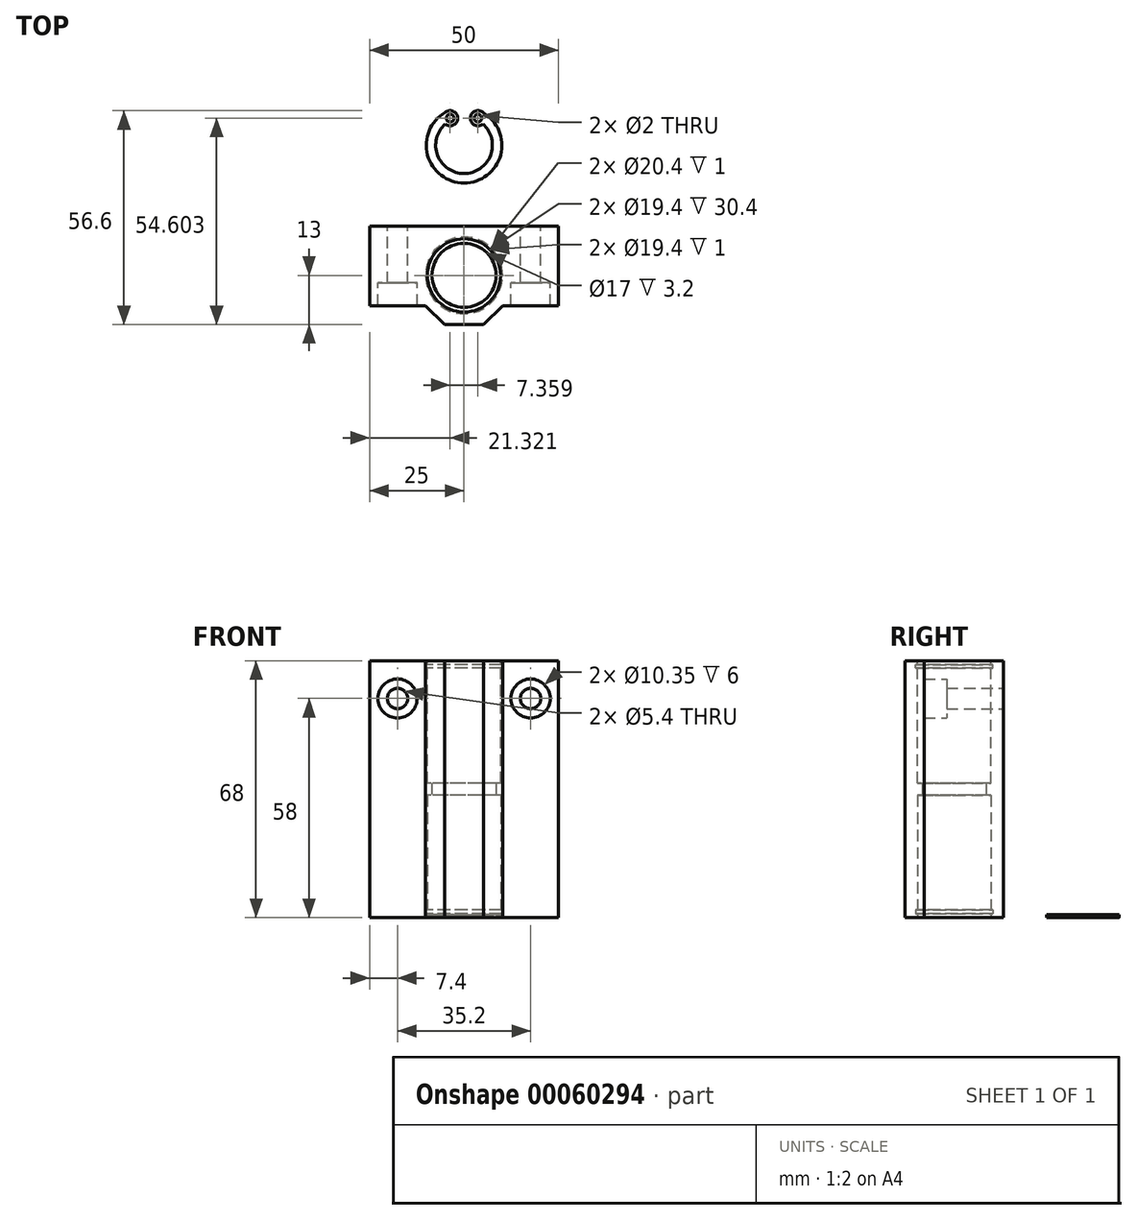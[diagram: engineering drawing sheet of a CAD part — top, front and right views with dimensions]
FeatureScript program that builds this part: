
annotation { "Feature Type Name" : "Feature", "Feature Type Description" : "" }
export const myFeature = defineFeature(function(context is Context, id is Id, definition is map)
    precondition{}
    {
        {
            var Q0;
            Q0=qCreatedBy(makeId("Top.planeOp"),FACE);
            var sketch = newSketch(context, id + "F0", { "sketchPlane" : qUnion([Q0])});
            skLineSegment(sketch, "E0.bottom", {"start": v(-25, 13) * mm, "end": v(25, 13) * mm});
            skLineSegment(sketch, "E0.top", {"start": v(-25, -13) * mm, "end": v(25, -13) * mm});
            skLineSegment(sketch, "E0.left", {"start": v(-25, 13) * mm, "end": v(-25, -13) * mm});
            skLineSegment(sketch, "E0.right", {"start": v(25, 13) * mm, "end": v(25, -13) * mm});
            skLineSegment(sketch, "E1", {"start": v(-25, 0) * mm, "end": v(25, 0) * mm});
            skLineSegment(sketch, "E2", {"start": v(-25, -8) * mm, "end": v(25, -8) * mm});
            skLineSegment(sketch, "E3", {"start": v(-25, 5) * mm, "end": v(-23, 3) * mm});
            skLineSegment(sketch, "E4", {"start": v(-23, 3) * mm, "end": v(-23, -13) * mm});
            skCircle(sketch, "E5", {"center": v(0, 0) * mm, "radius": 10.2 * mm});
            skLineSegment(sketch, "E6", {"start": v(0, 13) * mm, "end": v(0, -13) * mm});
            skLineSegment(sketch, "E7.MirrorCS", {"start": v(25, 5) * mm, "end": v(23, 3) * mm});
            skLineSegment(sketch, "E8.MirrorCS", {"start": v(23, 3) * mm, "end": v(23, -13) * mm});
            skLineSegment(sketch, "E9", {"start": v(-25, 5) * mm, "end": v(-25, 3) * mm});
            skLineSegment(sketch, "E10", {"start": v(25, 5) * mm, "end": v(25, 3) * mm});
            skLineSegment(sketch, "E11", {"start": v(-10.2, 13) * mm, "end": v(-10.2, -13) * mm});
            skLineSegment(sketch, "E12.MirrorCS", {"start": v(10.2, 13) * mm, "end": v(10.2, -13) * mm});
            skLineSegment(sketch, "E13", {"start": v(-10.2, -8) * mm, "end": v(-5.2, -13) * mm});
            skLineSegment(sketch, "E14.MirrorCS", {"start": v(10.2, -8) * mm, "end": v(5.2, -13) * mm});
            skCircle(sketch, "E15", {"center": v(0, 0) * mm, "radius": 9.7 * mm});
            skCircle(sketch, "E16", {"center": v(0, 0) * mm, "radius": 8.5 * mm});
            skSolve(sketch);
        }
        {
            var Q0;
            {var subQ0=sQuery(id+"F0.wireOp",EDGE,"E3");Q0=makeQuery(id+"F0.imprint","IMPRINT",FACE,{"disambiguationData":[TD([[makeQuery(id+"F0.imprint","IMPRINT",EDGE,{"derivedFrom":subQ0}),1.0]])]});}
            var Q1;
            {var subQ0=sQuery(id+"F0.wireOp",EDGE,"E6");var subQ1=sQuery(id+"F0.wireOp",EDGE,"E0.bottom");var subQ2=makeQuery(id+"F0.imprint","INTERSECT",VERTEX,{"derivedFrom":[subQ1,subQ0]});Q1=makeQuery(id+"F0.imprint","IMPRINT",FACE,{"disambiguationData":[TD([[makeQuery(id+"F0.imprint","IMPRINT",EDGE,{"disambiguationData":[TD([[subQ2,1.0]])],"derivedFrom":subQ1}),-1.0]])]});}
            var Q2;
            {var subQ0=sQuery(id+"F0.wireOp",EDGE,"E6");var subQ1=sQuery(id+"F0.wireOp",EDGE,"E0.bottom");var subQ2=makeQuery(id+"F0.imprint","INTERSECT",VERTEX,{"derivedFrom":[subQ1,subQ0]});Q2=makeQuery(id+"F0.imprint","IMPRINT",FACE,{"disambiguationData":[TD([[makeQuery(id+"F0.imprint","IMPRINT",EDGE,{"disambiguationData":[TD([[subQ2,-1.0]])],"derivedFrom":subQ1}),-1.0]])]});}
            var Q3;
            {var subQ0=sQuery(id+"F0.wireOp",EDGE,"E7.MirrorCS");Q3=makeQuery(id+"F0.imprint","IMPRINT",FACE,{"disambiguationData":[TD([[makeQuery(id+"F0.imprint","IMPRINT",EDGE,{"derivedFrom":subQ0}),-1.0]])]});}
            var Q4;
            {var subQ7=sQuery(id+"F0.wireOp",EDGE,"E13");Q4=makeQuery(id+"F0.imprint","IMPRINT",FACE,{"disambiguationData":[TD([[makeQuery(id+"F0.imprint","IMPRINT",EDGE,{"derivedFrom":subQ7}),1.0]])]});}
            var Q5;
            {var subQ0=sQuery(id+"F0.wireOp",EDGE,"E4");var subQ1=sQuery(id+"F0.wireOp",EDGE,"E1");var subQ2=makeQuery(id+"F0.imprint","INTERSECT",VERTEX,{"derivedFrom":[subQ1,subQ0]});Q5=makeQuery(id+"F0.imprint","IMPRINT",FACE,{"disambiguationData":[TD([[makeQuery(id+"F0.imprint","IMPRINT",EDGE,{"disambiguationData":[TD([[subQ2,-1.0]])],"derivedFrom":subQ0}),1.0]])]});}
            var Q6;
            {var subQ1=sQuery(id+"F0.wireOp",EDGE,"E2");var subQ3=sQuery(id+"F0.wireOp",EDGE,"E5");var subQ4=makeQuery(id+"F0.imprint","INTERSECT",VERTEX,{"disambiguationData":[OD(0.0)],"derivedFrom":[subQ1,subQ3]});Q6=makeQuery(id+"F0.imprint","IMPRINT",FACE,{"disambiguationData":[TD([[makeQuery(id+"F0.imprint","IMPRINT",EDGE,{"disambiguationData":[TD([[subQ4,1.0]])],"derivedFrom":subQ1}),1.0]])]});}
            var Q7;
            {var subQ0=sQuery(id+"F0.wireOp",EDGE,"E8.MirrorCS");var subQ1=sQuery(id+"F0.wireOp",EDGE,"E1");var subQ2=makeQuery(id+"F0.imprint","INTERSECT",VERTEX,{"derivedFrom":[subQ1,subQ0]});Q7=makeQuery(id+"F0.imprint","IMPRINT",FACE,{"disambiguationData":[TD([[makeQuery(id+"F0.imprint","IMPRINT",EDGE,{"disambiguationData":[TD([[subQ2,-1.0]])],"derivedFrom":subQ0}),-1.0]])]});}
            var Q8;
            {var subQ1=sQuery(id+"F0.wireOp",EDGE,"E2");var subQ3=sQuery(id+"F0.wireOp",EDGE,"E5");var subQ4=makeQuery(id+"F0.imprint","INTERSECT",VERTEX,{"disambiguationData":[OD(1.0)],"derivedFrom":[subQ1,subQ3]});Q8=makeQuery(id+"F0.imprint","IMPRINT",FACE,{"disambiguationData":[TD([[makeQuery(id+"F0.imprint","IMPRINT",EDGE,{"disambiguationData":[TD([[subQ4,-1.0]])],"derivedFrom":subQ1}),1.0]])]});}
            var Q9;
            {var subQ5=sQuery(id+"F0.wireOp",EDGE,"E14.MirrorCS");Q9=makeQuery(id+"F0.imprint","IMPRINT",FACE,{"disambiguationData":[TD([[makeQuery(id+"F0.imprint","IMPRINT",EDGE,{"derivedFrom":subQ5}),-1.0]])]});}
            var Q10;
            {var subQ3=sQuery(id+"F0.wireOp",EDGE,"E5");var subQ5=sQuery(id+"F0.wireOp",EDGE,"E2");var subQ6=makeQuery(id+"F0.imprint","INTERSECT",VERTEX,{"disambiguationData":[OD(0.0)],"derivedFrom":[subQ5,subQ3]});Q10=makeQuery(id+"F0.imprint","IMPRINT",FACE,{"disambiguationData":[TD([[makeQuery(id+"F0.imprint","IMPRINT",EDGE,{"disambiguationData":[TD([[subQ6,-1.0]])],"derivedFrom":subQ5}),1.0]])]});}
            var Q11;
            {var subQ0=sQuery(id+"F0.wireOp",EDGE,"E5");var subQ1=sQuery(id+"F0.wireOp",EDGE,"E2");var subQ2=makeQuery(id+"F0.imprint","INTERSECT",VERTEX,{"disambiguationData":[OD(0.0)],"derivedFrom":[subQ1,subQ0]});Q11=makeQuery(id+"F0.imprint","IMPRINT",FACE,{"disambiguationData":[TD([[makeQuery(id+"F0.imprint","IMPRINT",EDGE,{"disambiguationData":[TD([[subQ2,-1.0]])],"derivedFrom":subQ1}),-1.0]])]});}
            var Q12;
            {var subQ0=sQuery(id+"F0.wireOp",EDGE,"E15");var subQ1=sQuery(id+"F0.wireOp",EDGE,"E2");var subQ2=makeQuery(id+"F0.imprint","INTERSECT",VERTEX,{"disambiguationData":[OD(1.0)],"derivedFrom":[subQ1,subQ0]});Q12=makeQuery(id+"F0.imprint","IMPRINT",FACE,{"disambiguationData":[TD([[makeQuery(id+"F0.imprint","IMPRINT",EDGE,{"disambiguationData":[TD([[subQ2,-1.0]])],"derivedFrom":subQ1}),-1.0]])]});}
            var Q13;
            {var subQ0=sQuery(id+"F0.wireOp",EDGE,"E15");var subQ5=sQuery(id+"F0.wireOp",EDGE,"E2");var subQ6=makeQuery(id+"F0.imprint","INTERSECT",VERTEX,{"disambiguationData":[OD(1.0)],"derivedFrom":[subQ5,subQ0]});Q13=makeQuery(id+"F0.imprint","IMPRINT",FACE,{"disambiguationData":[TD([[makeQuery(id+"F0.imprint","IMPRINT",EDGE,{"disambiguationData":[TD([[subQ6,-1.0]])],"derivedFrom":subQ5}),1.0]])]});}
            var Q14;
            {var subQ3=sQuery(id+"F0.wireOp",EDGE,"E5");var subQ5=sQuery(id+"F0.wireOp",EDGE,"E6");var subQ6=makeQuery(id+"F0.imprint","INTERSECT",VERTEX,{"disambiguationData":[OD(0.0)],"derivedFrom":[subQ3,subQ5]});Q14=makeQuery(id+"F0.imprint","IMPRINT",FACE,{"disambiguationData":[TD([[makeQuery(id+"F0.imprint","IMPRINT",EDGE,{"disambiguationData":[TD([[subQ6,-1.0]])],"derivedFrom":subQ5}),1.0]])]});}
            var Q15;
            {var subQ3=sQuery(id+"F0.wireOp",EDGE,"E5");var subQ5=sQuery(id+"F0.wireOp",EDGE,"E6");var subQ6=makeQuery(id+"F0.imprint","INTERSECT",VERTEX,{"disambiguationData":[OD(0.0)],"derivedFrom":[subQ3,subQ5]});Q15=makeQuery(id+"F0.imprint","IMPRINT",FACE,{"disambiguationData":[TD([[makeQuery(id+"F0.imprint","IMPRINT",EDGE,{"disambiguationData":[TD([[subQ6,-1.0]])],"derivedFrom":subQ5}),-1.0]])]});}
            var Q16;
            {var subQ0=sQuery(id+"F0.wireOp",EDGE,"E15");var subQ1=sQuery(id+"F0.wireOp",EDGE,"E1");var subQ2=makeQuery(id+"F0.imprint","INTERSECT",VERTEX,{"disambiguationData":[OD(0.0)],"derivedFrom":[subQ1,subQ0]});Q16=makeQuery(id+"F0.imprint","IMPRINT",FACE,{"disambiguationData":[TD([[makeQuery(id+"F0.imprint","IMPRINT",EDGE,{"disambiguationData":[TD([[subQ2,-1.0]])],"derivedFrom":subQ1}),1.0]])]});}
            var Q17;
            {var subQ0=sQuery(id+"F0.wireOp",EDGE,"E15");var subQ1=sQuery(id+"F0.wireOp",EDGE,"E1");var subQ2=makeQuery(id+"F0.imprint","INTERSECT",VERTEX,{"disambiguationData":[OD(0.0)],"derivedFrom":[subQ1,subQ0]});Q17=makeQuery(id+"F0.imprint","IMPRINT",FACE,{"disambiguationData":[TD([[makeQuery(id+"F0.imprint","IMPRINT",EDGE,{"disambiguationData":[TD([[subQ2,-1.0]])],"derivedFrom":subQ1}),-1.0]])]});}
            var Q18;
            {var subQ0=sQuery(id+"F0.wireOp",EDGE,"E15");var subQ1=sQuery(id+"F0.wireOp",EDGE,"E2");var subQ2=makeQuery(id+"F0.imprint","INTERSECT",VERTEX,{"disambiguationData":[OD(0.0)],"derivedFrom":[subQ1,subQ0]});Q18=makeQuery(id+"F0.imprint","IMPRINT",FACE,{"disambiguationData":[TD([[makeQuery(id+"F0.imprint","IMPRINT",EDGE,{"disambiguationData":[TD([[subQ2,-1.0]])],"derivedFrom":subQ1}),-1.0]])]});}
            var Q19;
            {var subQ0=sQuery(id+"F0.wireOp",EDGE,"E16");var subQ1=sQuery(id+"F0.wireOp",EDGE,"E2");var subQ2=makeQuery(id+"F0.imprint","INTERSECT",VERTEX,{"disambiguationData":[OD(1.0)],"derivedFrom":[subQ1,subQ0]});Q19=makeQuery(id+"F0.imprint","IMPRINT",FACE,{"disambiguationData":[TD([[makeQuery(id+"F0.imprint","IMPRINT",EDGE,{"disambiguationData":[TD([[subQ2,-1.0]])],"derivedFrom":subQ1}),-1.0]])]});}
            var Q20;
            {var subQ0=sQuery(id+"F0.wireOp",EDGE,"E16");var subQ1=sQuery(id+"F0.wireOp",EDGE,"E1");var subQ2=makeQuery(id+"F0.imprint","INTERSECT",VERTEX,{"disambiguationData":[OD(1.0)],"derivedFrom":[subQ1,subQ0]});Q20=makeQuery(id+"F0.imprint","IMPRINT",FACE,{"disambiguationData":[TD([[makeQuery(id+"F0.imprint","IMPRINT",EDGE,{"disambiguationData":[TD([[subQ2,-1.0]])],"derivedFrom":subQ1}),-1.0]])]});}
            var Q21;
            {var subQ0=sQuery(id+"F0.wireOp",EDGE,"E16");var subQ1=sQuery(id+"F0.wireOp",EDGE,"E1");var subQ2=makeQuery(id+"F0.imprint","INTERSECT",VERTEX,{"disambiguationData":[OD(1.0)],"derivedFrom":[subQ1,subQ0]});Q21=makeQuery(id+"F0.imprint","IMPRINT",FACE,{"disambiguationData":[TD([[makeQuery(id+"F0.imprint","IMPRINT",EDGE,{"disambiguationData":[TD([[subQ2,-1.0]])],"derivedFrom":subQ1}),1.0]])]});}
            var Q22;
            {var subQ0=sQuery(id+"F0.wireOp",EDGE,"E1");var subQ1=sQuery(id+"F0.wireOp",EDGE,"E0.right");var subQ2=makeQuery(id+"F0.imprint","INTERSECT",VERTEX,{"derivedFrom":[subQ1,subQ0]});Q22=makeQuery(id+"F0.imprint","IMPRINT",FACE,{"disambiguationData":[TD([[makeQuery(id+"F0.imprint","IMPRINT",EDGE,{"disambiguationData":[TD([[subQ2,-1.0]])],"derivedFrom":subQ1}),-1.0]])]});}
            var Q23;
            {var subQ1=sQuery(id+"F0.wireOp",EDGE,"E7.MirrorCS");Q23=makeQuery(id+"F0.imprint","IMPRINT",FACE,{"disambiguationData":[TD([[makeQuery(id+"F0.imprint","IMPRINT",EDGE,{"derivedFrom":subQ1}),1.0]])]});}
            var Q24;
            {var subQ0=sQuery(id+"F0.wireOp",EDGE,"E1");var subQ1=sQuery(id+"F0.wireOp",EDGE,"E0.left");var subQ2=makeQuery(id+"F0.imprint","INTERSECT",VERTEX,{"derivedFrom":[subQ1,subQ0]});Q24=makeQuery(id+"F0.imprint","IMPRINT",FACE,{"disambiguationData":[TD([[makeQuery(id+"F0.imprint","IMPRINT",EDGE,{"disambiguationData":[TD([[subQ2,-1.0]])],"derivedFrom":subQ1}),1.0]])]});}
            var Q25;
            {var subQ5=sQuery(id+"F0.wireOp",EDGE,"E3");Q25=makeQuery(id+"F0.imprint","IMPRINT",FACE,{"disambiguationData":[TD([[makeQuery(id+"F0.imprint","IMPRINT",EDGE,{"derivedFrom":subQ5}),-1.0]])]});}
            extrude(context, id + "F1", {"entities" : qUnion([Q0, Q1, Q2, Q3, Q4, Q5, Q6, Q7, Q8, Q9, Q10, Q11, Q12, Q13, Q14, Q15, Q16, Q17, Q18, Q19, Q20, Q21, Q22, Q23, Q24, Q25]), "depth" : 68 * mm});
        }
        {
            var Q0;
            {var subQ0=sQuery(id+"F0.wireOp",EDGE,"E15");var subQ1=sQuery(id+"F0.wireOp",EDGE,"E1");var subQ2=makeQuery(id+"F0.imprint","INTERSECT",VERTEX,{"disambiguationData":[OD(0.0)],"derivedFrom":[subQ1,subQ0]});Q0=makeQuery(id+"F0.imprint","IMPRINT",FACE,{"disambiguationData":[TD([[makeQuery(id+"F0.imprint","IMPRINT",EDGE,{"disambiguationData":[TD([[subQ2,-1.0]])],"derivedFrom":subQ1}),-1.0]])]});}
            var Q1;
            {var subQ0=sQuery(id+"F0.wireOp",EDGE,"E15");var subQ1=sQuery(id+"F0.wireOp",EDGE,"E2");var subQ2=makeQuery(id+"F0.imprint","INTERSECT",VERTEX,{"disambiguationData":[OD(0.0)],"derivedFrom":[subQ1,subQ0]});Q1=makeQuery(id+"F0.imprint","IMPRINT",FACE,{"disambiguationData":[TD([[makeQuery(id+"F0.imprint","IMPRINT",EDGE,{"disambiguationData":[TD([[subQ2,-1.0]])],"derivedFrom":subQ1}),-1.0]])]});}
            var Q2;
            {var subQ0=sQuery(id+"F0.wireOp",EDGE,"E16");var subQ1=sQuery(id+"F0.wireOp",EDGE,"E2");var subQ2=makeQuery(id+"F0.imprint","INTERSECT",VERTEX,{"disambiguationData":[OD(1.0)],"derivedFrom":[subQ1,subQ0]});Q2=makeQuery(id+"F0.imprint","IMPRINT",FACE,{"disambiguationData":[TD([[makeQuery(id+"F0.imprint","IMPRINT",EDGE,{"disambiguationData":[TD([[subQ2,-1.0]])],"derivedFrom":subQ1}),-1.0]])]});}
            var Q3;
            {var subQ0=sQuery(id+"F0.wireOp",EDGE,"E16");var subQ1=sQuery(id+"F0.wireOp",EDGE,"E1");var subQ2=makeQuery(id+"F0.imprint","INTERSECT",VERTEX,{"disambiguationData":[OD(1.0)],"derivedFrom":[subQ1,subQ0]});Q3=makeQuery(id+"F0.imprint","IMPRINT",FACE,{"disambiguationData":[TD([[makeQuery(id+"F0.imprint","IMPRINT",EDGE,{"disambiguationData":[TD([[subQ2,-1.0]])],"derivedFrom":subQ1}),-1.0]])]});}
            var Q4;
            {var subQ0=sQuery(id+"F0.wireOp",EDGE,"E16");var subQ1=sQuery(id+"F0.wireOp",EDGE,"E1");var subQ2=makeQuery(id+"F0.imprint","INTERSECT",VERTEX,{"disambiguationData":[OD(1.0)],"derivedFrom":[subQ1,subQ0]});Q4=makeQuery(id+"F0.imprint","IMPRINT",FACE,{"disambiguationData":[TD([[makeQuery(id+"F0.imprint","IMPRINT",EDGE,{"disambiguationData":[TD([[subQ2,-1.0]])],"derivedFrom":subQ1}),1.0]])]});}
            var Q5;
            {var subQ0=sQuery(id+"F0.wireOp",EDGE,"E15");var subQ1=sQuery(id+"F0.wireOp",EDGE,"E1");var subQ2=makeQuery(id+"F0.imprint","INTERSECT",VERTEX,{"disambiguationData":[OD(0.0)],"derivedFrom":[subQ1,subQ0]});Q5=makeQuery(id+"F0.imprint","IMPRINT",FACE,{"disambiguationData":[TD([[makeQuery(id+"F0.imprint","IMPRINT",EDGE,{"disambiguationData":[TD([[subQ2,-1.0]])],"derivedFrom":subQ1}),1.0]])]});}
            extrude(context, id + "F2", {"entities" : qUnion([Q0, Q1, Q2, Q3, Q4, Q5]), "operationType" : NewBodyOperationType.REMOVE, "depth" : 32.4 * mm});
        }
        {
            var Q0;
            {var subQ0=sQuery(id+"F0.wireOp",EDGE,"E15");var subQ1=sQuery(id+"F0.wireOp",EDGE,"E2");var subQ2=makeQuery(id+"F0.imprint","INTERSECT",VERTEX,{"disambiguationData":[OD(1.0)],"derivedFrom":[subQ1,subQ0]});Q0=makeQuery(id+"F0.imprint","IMPRINT",FACE,{"disambiguationData":[TD([[makeQuery(id+"F0.imprint","IMPRINT",EDGE,{"disambiguationData":[TD([[subQ2,-1.0]])],"derivedFrom":subQ1}),-1.0]])]});}
            var Q1;
            {var subQ0=sQuery(id+"F0.wireOp",EDGE,"E15");var subQ5=sQuery(id+"F0.wireOp",EDGE,"E2");var subQ6=makeQuery(id+"F0.imprint","INTERSECT",VERTEX,{"disambiguationData":[OD(1.0)],"derivedFrom":[subQ5,subQ0]});Q1=makeQuery(id+"F0.imprint","IMPRINT",FACE,{"disambiguationData":[TD([[makeQuery(id+"F0.imprint","IMPRINT",EDGE,{"disambiguationData":[TD([[subQ6,-1.0]])],"derivedFrom":subQ5}),1.0]])]});}
            var Q2;
            {var subQ3=sQuery(id+"F0.wireOp",EDGE,"E5");var subQ5=sQuery(id+"F0.wireOp",EDGE,"E6");var subQ7=makeQuery(id+"F0.imprint","INTERSECT",VERTEX,{"disambiguationData":[OD(0.0)],"derivedFrom":[subQ3,subQ5]});Q2=makeQuery(id+"F0.imprint","IMPRINT",FACE,{"disambiguationData":[TD([[makeQuery(id+"F0.imprint","IMPRINT",EDGE,{"disambiguationData":[TD([[subQ7,-1.0]])],"derivedFrom":subQ5}),1.0]])]});}
            var Q3;
            {var subQ3=sQuery(id+"F0.wireOp",EDGE,"E5");var subQ5=sQuery(id+"F0.wireOp",EDGE,"E6");var subQ6=makeQuery(id+"F0.imprint","INTERSECT",VERTEX,{"disambiguationData":[OD(0.0)],"derivedFrom":[subQ3,subQ5]});Q3=makeQuery(id+"F0.imprint","IMPRINT",FACE,{"disambiguationData":[TD([[makeQuery(id+"F0.imprint","IMPRINT",EDGE,{"disambiguationData":[TD([[subQ6,-1.0]])],"derivedFrom":subQ5}),-1.0]])]});}
            var Q4;
            {var subQ3=sQuery(id+"F0.wireOp",EDGE,"E5");var subQ5=sQuery(id+"F0.wireOp",EDGE,"E2");var subQ6=makeQuery(id+"F0.imprint","INTERSECT",VERTEX,{"disambiguationData":[OD(0.0)],"derivedFrom":[subQ5,subQ3]});Q4=makeQuery(id+"F0.imprint","IMPRINT",FACE,{"disambiguationData":[TD([[makeQuery(id+"F0.imprint","IMPRINT",EDGE,{"disambiguationData":[TD([[subQ6,-1.0]])],"derivedFrom":subQ5}),1.0]])]});}
            var Q5;
            {var subQ0=sQuery(id+"F0.wireOp",EDGE,"E5");var subQ1=sQuery(id+"F0.wireOp",EDGE,"E2");var subQ2=makeQuery(id+"F0.imprint","INTERSECT",VERTEX,{"disambiguationData":[OD(0.0)],"derivedFrom":[subQ1,subQ0]});Q5=makeQuery(id+"F0.imprint","IMPRINT",FACE,{"disambiguationData":[TD([[makeQuery(id+"F0.imprint","IMPRINT",EDGE,{"disambiguationData":[TD([[subQ2,-1.0]])],"derivedFrom":subQ1}),-1.0]])]});}
            extrude(context, id + "F3", {"entities" : qUnion([Q0, Q1, Q2, Q3, Q4, Q5]), "operationType" : NewBodyOperationType.REMOVE, "depth" : 2 * mm});
        }
        {
            var Q0;
            {var subQ3=sQuery(id+"F0.wireOp",EDGE,"E5");var subQ5=sQuery(id+"F0.wireOp",EDGE,"E2");var subQ6=makeQuery(id+"F0.imprint","INTERSECT",VERTEX,{"disambiguationData":[OD(0.0)],"derivedFrom":[subQ5,subQ3]});Q0=makeQuery(id+"F0.imprint","IMPRINT",FACE,{"disambiguationData":[TD([[makeQuery(id+"F0.imprint","IMPRINT",EDGE,{"disambiguationData":[TD([[subQ6,-1.0]])],"derivedFrom":subQ5}),1.0]])]});}
            var Q1;
            {var subQ0=sQuery(id+"F0.wireOp",EDGE,"E5");var subQ1=sQuery(id+"F0.wireOp",EDGE,"E2");var subQ2=makeQuery(id+"F0.imprint","INTERSECT",VERTEX,{"disambiguationData":[OD(0.0)],"derivedFrom":[subQ1,subQ0]});Q1=makeQuery(id+"F0.imprint","IMPRINT",FACE,{"disambiguationData":[TD([[makeQuery(id+"F0.imprint","IMPRINT",EDGE,{"disambiguationData":[TD([[subQ2,-1.0]])],"derivedFrom":subQ1}),-1.0]])]});}
            var Q2;
            {var subQ0=sQuery(id+"F0.wireOp",EDGE,"E15");var subQ1=sQuery(id+"F0.wireOp",EDGE,"E2");var subQ2=makeQuery(id+"F0.imprint","INTERSECT",VERTEX,{"disambiguationData":[OD(1.0)],"derivedFrom":[subQ1,subQ0]});Q2=makeQuery(id+"F0.imprint","IMPRINT",FACE,{"disambiguationData":[TD([[makeQuery(id+"F0.imprint","IMPRINT",EDGE,{"disambiguationData":[TD([[subQ2,-1.0]])],"derivedFrom":subQ1}),-1.0]])]});}
            var Q3;
            {var subQ0=sQuery(id+"F0.wireOp",EDGE,"E15");var subQ5=sQuery(id+"F0.wireOp",EDGE,"E2");var subQ6=makeQuery(id+"F0.imprint","INTERSECT",VERTEX,{"disambiguationData":[OD(1.0)],"derivedFrom":[subQ5,subQ0]});Q3=makeQuery(id+"F0.imprint","IMPRINT",FACE,{"disambiguationData":[TD([[makeQuery(id+"F0.imprint","IMPRINT",EDGE,{"disambiguationData":[TD([[subQ6,-1.0]])],"derivedFrom":subQ5}),1.0]])]});}
            var Q4;
            {var subQ3=sQuery(id+"F0.wireOp",EDGE,"E5");var subQ5=sQuery(id+"F0.wireOp",EDGE,"E6");var subQ7=makeQuery(id+"F0.imprint","INTERSECT",VERTEX,{"disambiguationData":[OD(0.0)],"derivedFrom":[subQ3,subQ5]});Q4=makeQuery(id+"F0.imprint","IMPRINT",FACE,{"disambiguationData":[TD([[makeQuery(id+"F0.imprint","IMPRINT",EDGE,{"disambiguationData":[TD([[subQ7,-1.0]])],"derivedFrom":subQ5}),1.0]])]});}
            var Q5;
            {var subQ3=sQuery(id+"F0.wireOp",EDGE,"E5");var subQ5=sQuery(id+"F0.wireOp",EDGE,"E6");var subQ6=makeQuery(id+"F0.imprint","INTERSECT",VERTEX,{"disambiguationData":[OD(0.0)],"derivedFrom":[subQ3,subQ5]});Q5=makeQuery(id+"F0.imprint","IMPRINT",FACE,{"disambiguationData":[TD([[makeQuery(id+"F0.imprint","IMPRINT",EDGE,{"disambiguationData":[TD([[subQ6,-1.0]])],"derivedFrom":subQ5}),-1.0]])]});}
            extrude(context, id + "F4", {"entities" : qUnion([Q0, Q1, Q2, Q3, Q4, Q5]), "operationType" : NewBodyOperationType.ADD, "depth" : 1 * mm});
        }
        {
            var Q0;
            Q0=makeQuery(id+"F1.opExtrude","CAP_FACE",FACE,{"disambiguationData":[OSD([sQuery(id+"F0.wireOp",EDGE,"E0.bottom"),sQuery(id+"F0.wireOp",EDGE,"E0.top"),sQuery(id+"F0.wireOp",EDGE,"E0.left"),sQuery(id+"F0.wireOp",EDGE,"E0.right"),sQuery(id+"F0.wireOp",EDGE,"E2"),sQuery(id+"F0.wireOp",EDGE,"E3"),sQuery(id+"F0.wireOp",EDGE,"E4"),sQuery(id+"F0.wireOp",EDGE,"E7.MirrorCS"),sQuery(id+"F0.wireOp",EDGE,"E8.MirrorCS"),sQuery(id+"F0.wireOp",EDGE,"E13"),sQuery(id+"F0.wireOp",EDGE,"E14.MirrorCS"),sQuery(id+"F0.wireOp",EDGE,"E16")])],"isStart":false});
            var sketch = newSketch(context, id + "F5", { "sketchPlane" : qUnion([Q0])});
            skCircle(sketch, "E17", {"center": v(0, 0) * mm, "radius": 10.2 * mm});
            skCircle(sketch, "E18", {"center": v(0, 0) * mm, "radius": 9.7 * mm});
            skCircle(sketch, "E19", {"center": v(0, 0) * mm, "radius": 8.5 * mm});
            skSolve(sketch);
        }
        {
            var Q0;
            Q0=makeQuery(id+"F5.imprint","IMPRINT",FACE,{"disambiguationData":[TD([[makeQuery(id+"F5.imprint","IMPRINT",EDGE,{"derivedFrom":sQuery(id+"F5.wireOp",EDGE,"E18")}),1.0]])]});
            extrude(context, id + "F6", {"entities" : qUnion([Q0]), "operationType" : NewBodyOperationType.REMOVE, "oppositeDirection" : true, "depth" : 32.4 * mm});
        }
        {
            var Q0;
            Q0=makeQuery(id+"F5.imprint","IMPRINT",FACE,{"disambiguationData":[TD([[makeQuery(id+"F5.imprint","IMPRINT",EDGE,{"derivedFrom":sQuery(id+"F5.wireOp",EDGE,"E17")}),1.0]])]});
            extrude(context, id + "F7", {"entities" : qUnion([Q0]), "operationType" : NewBodyOperationType.REMOVE, "oppositeDirection" : true, "depth" : 2 * mm});
        }
        {
            var Q0;
            Q0=makeQuery(id+"F5.imprint","IMPRINT",FACE,{"disambiguationData":[TD([[makeQuery(id+"F5.imprint","IMPRINT",EDGE,{"derivedFrom":sQuery(id+"F5.wireOp",EDGE,"E17")}),1.0]])]});
            extrude(context, id + "F8", {"entities" : qUnion([Q0]), "operationType" : NewBodyOperationType.ADD, "oppositeDirection" : true, "depth" : 1 * mm});
        }
        {
            var Q0;
            Q0=makeQuery(id+"F1.opExtrude","SWEPT_FACE",FACE,{"disambiguationData":[OSD([sQuery(id+"F0.wireOp",EDGE,"E0.bottom")])]});
            var sketch = newSketch(context, id + "F9", { "sketchPlane" : qUnion([Q0])});
            skLineSegment(sketch, "E20.bottom", {"start": v(-25, 68) * mm, "end": v(25, 68) * mm});
            skLineSegment(sketch, "E20.top", {"start": v(-25, 48) * mm, "end": v(25, 48) * mm});
            skLineSegment(sketch, "E20.left", {"start": v(-25, 68) * mm, "end": v(-25, 48) * mm});
            skLineSegment(sketch, "E20.right", {"start": v(25, 68) * mm, "end": v(25, 48) * mm});
            skLineSegment(sketch, "E21", {"start": v(0, 68) * mm, "end": v(0, 48) * mm});
            skLineSegment(sketch, "E22", {"start": v(-17.6, 68) * mm, "end": v(-17.6, 48) * mm});
            skLineSegment(sketch, "E23.MirrorCS", {"start": v(17.6, 68) * mm, "end": v(17.6, 48) * mm});
            skCircle(sketch, "E24", {"center": v(-17.6, 58) * mm, "radius": 2.7 * mm});
            skCircle(sketch, "E25.MirrorC", {"center": v(17.6, 58) * mm, "radius": 2.7 * mm});
            skCircle(sketch, "E26", {"center": v(-17.6, 58) * mm, "radius": 5.17 * mm});
            skCircle(sketch, "E27.MirrorC", {"center": v(17.6, 58) * mm, "radius": 5.17 * mm});
            skSolve(sketch);
        }
        {
            var Q0;
            {var subQ0=sQuery(id+"F9.wireOp",EDGE,"E26");var subQ1=sQuery(id+"F9.wireOp",EDGE,"E22");var subQ2=makeQuery(id+"F9.imprint","INTERSECT",VERTEX,{"disambiguationData":[OD(0.0)],"derivedFrom":[subQ1,subQ0]});Q0=makeQuery(id+"F9.imprint","IMPRINT",FACE,{"disambiguationData":[TD([[makeQuery(id+"F9.imprint","IMPRINT",EDGE,{"disambiguationData":[TD([[subQ2,-1.0]])],"derivedFrom":subQ1}),1.0]])]});}
            var Q1;
            {var subQ0=sQuery(id+"F9.wireOp",EDGE,"E26");var subQ1=sQuery(id+"F9.wireOp",EDGE,"E22");var subQ2=makeQuery(id+"F9.imprint","INTERSECT",VERTEX,{"disambiguationData":[OD(0.0)],"derivedFrom":[subQ1,subQ0]});Q1=makeQuery(id+"F9.imprint","IMPRINT",FACE,{"disambiguationData":[TD([[makeQuery(id+"F9.imprint","IMPRINT",EDGE,{"disambiguationData":[TD([[subQ2,-1.0]])],"derivedFrom":subQ1}),-1.0]])]});}
            var Q2;
            {var subQ0=sQuery(id+"F9.wireOp",EDGE,"E27.MirrorC");var subQ1=sQuery(id+"F9.wireOp",EDGE,"E23.MirrorCS");var subQ2=makeQuery(id+"F9.imprint","INTERSECT",VERTEX,{"disambiguationData":[OD(0.0)],"derivedFrom":[subQ1,subQ0]});Q2=makeQuery(id+"F9.imprint","IMPRINT",FACE,{"disambiguationData":[TD([[makeQuery(id+"F9.imprint","IMPRINT",EDGE,{"disambiguationData":[TD([[subQ2,-1.0]])],"derivedFrom":subQ1}),-1.0]])]});}
            var Q3;
            {var subQ0=sQuery(id+"F9.wireOp",EDGE,"E27.MirrorC");var subQ1=sQuery(id+"F9.wireOp",EDGE,"E23.MirrorCS");var subQ2=makeQuery(id+"F9.imprint","INTERSECT",VERTEX,{"disambiguationData":[OD(0.0)],"derivedFrom":[subQ1,subQ0]});Q3=makeQuery(id+"F9.imprint","IMPRINT",FACE,{"disambiguationData":[TD([[makeQuery(id+"F9.imprint","IMPRINT",EDGE,{"disambiguationData":[TD([[subQ2,-1.0]])],"derivedFrom":subQ1}),1.0]])]});}
            var Q4;
            {var subQ0=sQuery(id+"F9.wireOp",EDGE,"E25.MirrorC");var subQ1=sQuery(id+"F9.wireOp",EDGE,"E23.MirrorCS");var subQ2=makeQuery(id+"F9.imprint","INTERSECT",VERTEX,{"disambiguationData":[OD(0.0)],"derivedFrom":[subQ1,subQ0]});Q4=makeQuery(id+"F9.imprint","IMPRINT",FACE,{"disambiguationData":[TD([[makeQuery(id+"F9.imprint","IMPRINT",EDGE,{"disambiguationData":[TD([[subQ2,-1.0]])],"derivedFrom":subQ1}),-1.0]])]});}
            var Q5;
            {var subQ0=sQuery(id+"F9.wireOp",EDGE,"E25.MirrorC");var subQ1=sQuery(id+"F9.wireOp",EDGE,"E23.MirrorCS");var subQ2=makeQuery(id+"F9.imprint","INTERSECT",VERTEX,{"disambiguationData":[OD(0.0)],"derivedFrom":[subQ1,subQ0]});Q5=makeQuery(id+"F9.imprint","IMPRINT",FACE,{"disambiguationData":[TD([[makeQuery(id+"F9.imprint","IMPRINT",EDGE,{"disambiguationData":[TD([[subQ2,-1.0]])],"derivedFrom":subQ1}),1.0]])]});}
            var Q6;
            {var subQ0=sQuery(id+"F9.wireOp",EDGE,"E24");var subQ1=sQuery(id+"F9.wireOp",EDGE,"E22");var subQ2=makeQuery(id+"F9.imprint","INTERSECT",VERTEX,{"disambiguationData":[OD(0.0)],"derivedFrom":[subQ1,subQ0]});Q6=makeQuery(id+"F9.imprint","IMPRINT",FACE,{"disambiguationData":[TD([[makeQuery(id+"F9.imprint","IMPRINT",EDGE,{"disambiguationData":[TD([[subQ2,-1.0]])],"derivedFrom":subQ1}),1.0]])]});}
            var Q7;
            {var subQ0=sQuery(id+"F9.wireOp",EDGE,"E24");var subQ1=sQuery(id+"F9.wireOp",EDGE,"E22");var subQ2=makeQuery(id+"F9.imprint","INTERSECT",VERTEX,{"disambiguationData":[OD(0.0)],"derivedFrom":[subQ1,subQ0]});Q7=makeQuery(id+"F9.imprint","IMPRINT",FACE,{"disambiguationData":[TD([[makeQuery(id+"F9.imprint","IMPRINT",EDGE,{"disambiguationData":[TD([[subQ2,-1.0]])],"derivedFrom":subQ1}),-1.0]])]});}
            extrude(context, id + "F10", {"entities" : qUnion([Q0, Q1, Q2, Q3, Q4, Q5, Q6, Q7]), "operationType" : NewBodyOperationType.REMOVE, "oppositeDirection" : true, "depth" : 21 * mm});
        }
        {
            var Q0;
            {var subQ0=sQuery(id+"F9.wireOp",EDGE,"E26");var subQ1=sQuery(id+"F9.wireOp",EDGE,"E22");var subQ2=makeQuery(id+"F9.imprint","INTERSECT",VERTEX,{"disambiguationData":[OD(0.0)],"derivedFrom":[subQ1,subQ0]});Q0=makeQuery(id+"F9.imprint","IMPRINT",FACE,{"disambiguationData":[TD([[makeQuery(id+"F9.imprint","IMPRINT",EDGE,{"disambiguationData":[TD([[subQ2,-1.0]])],"derivedFrom":subQ1}),-1.0]])]});}
            var Q1;
            {var subQ0=sQuery(id+"F9.wireOp",EDGE,"E26");var subQ1=sQuery(id+"F9.wireOp",EDGE,"E22");var subQ2=makeQuery(id+"F9.imprint","INTERSECT",VERTEX,{"disambiguationData":[OD(0.0)],"derivedFrom":[subQ1,subQ0]});Q1=makeQuery(id+"F9.imprint","IMPRINT",FACE,{"disambiguationData":[TD([[makeQuery(id+"F9.imprint","IMPRINT",EDGE,{"disambiguationData":[TD([[subQ2,-1.0]])],"derivedFrom":subQ1}),1.0]])]});}
            var Q2;
            {var subQ0=sQuery(id+"F9.wireOp",EDGE,"E27.MirrorC");var subQ1=sQuery(id+"F9.wireOp",EDGE,"E23.MirrorCS");var subQ2=makeQuery(id+"F9.imprint","INTERSECT",VERTEX,{"disambiguationData":[OD(0.0)],"derivedFrom":[subQ1,subQ0]});Q2=makeQuery(id+"F9.imprint","IMPRINT",FACE,{"disambiguationData":[TD([[makeQuery(id+"F9.imprint","IMPRINT",EDGE,{"disambiguationData":[TD([[subQ2,-1.0]])],"derivedFrom":subQ1}),-1.0]])]});}
            var Q3;
            {var subQ0=sQuery(id+"F9.wireOp",EDGE,"E27.MirrorC");var subQ1=sQuery(id+"F9.wireOp",EDGE,"E23.MirrorCS");var subQ2=makeQuery(id+"F9.imprint","INTERSECT",VERTEX,{"disambiguationData":[OD(0.0)],"derivedFrom":[subQ1,subQ0]});Q3=makeQuery(id+"F9.imprint","IMPRINT",FACE,{"disambiguationData":[TD([[makeQuery(id+"F9.imprint","IMPRINT",EDGE,{"disambiguationData":[TD([[subQ2,-1.0]])],"derivedFrom":subQ1}),1.0]])]});}
            extrude(context, id + "F11", {"entities" : qUnion([Q0, Q1, Q2, Q3]), "operationType" : NewBodyOperationType.ADD, "oppositeDirection" : true, "depth" : 15 * mm});
        }
        {
            var Q0;
            Q0=qCreatedBy(makeId("Top.planeOp"),FACE);
            var sketch = newSketch(context, id + "F12", { "sketchPlane" : qUnion([Q0])});
            skArc(sketch, "E28", {"start": v(-5, 43.1) * mm, "mid": v(0, 24.44) * mm, "end": v(5, 43.1) * mm});
            skArc(sketch, "E29", {"start": v(-5, 40.03) * mm, "mid": v(0, 26.94) * mm, "end": v(5, 40.03) * mm});
            skLineSegment(sketch, "E30", {"start": v(-5, 40.03) * mm, "end": v(-5, 40.1) * mm});
            skLineSegment(sketch, "E31.MirrorCS", {"start": v(5, 40.03) * mm, "end": v(5, 40.1) * mm});
            skArc(sketch, "E32", {"start": v(5, 43.1) * mm, "mid": v(1.68, 41.6) * mm, "end": v(5, 40.1) * mm});
            skCircle(sketch, "E33", {"center": v(3.68, 41.6) * mm, "radius": 1 * mm});
            skArc(sketch, "E34.MirrorC", {"start": v(-5, 43.1) * mm, "mid": v(-1.68, 41.6) * mm, "end": v(-5, 40.1) * mm});
            skCircle(sketch, "E35.MirrorC", {"center": v(-3.68, 41.6) * mm, "radius": 1 * mm});
            skSolve(sketch);
        }
        {
            var Q0;
            Q0 = qSketchRegion(id + "F12", true);
            extrude(context, id + "F13", {"entities" : qUnion([Q0]), "depth" : 0.8 * mm});
        }
    });
